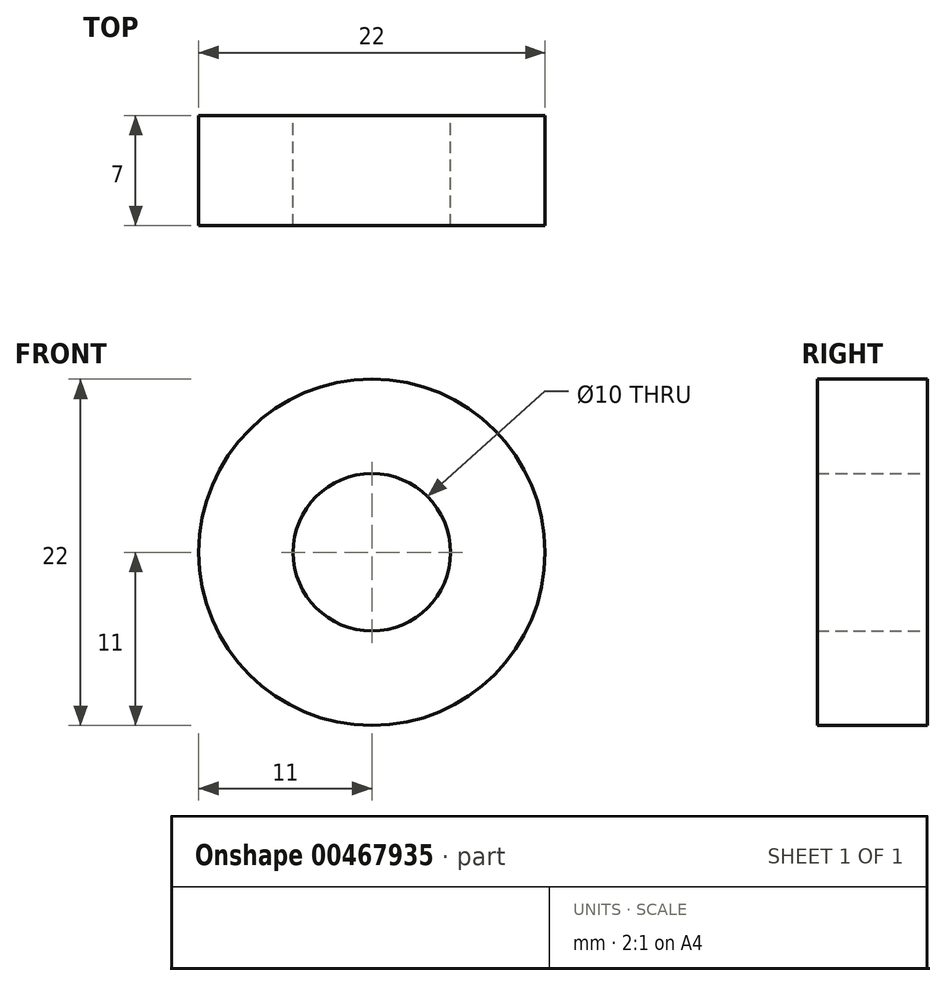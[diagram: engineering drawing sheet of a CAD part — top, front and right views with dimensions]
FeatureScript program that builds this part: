
annotation { "Feature Type Name" : "Feature", "Feature Type Description" : "" }
export const myFeature = defineFeature(function(context is Context, id is Id, definition is map)
    precondition{}
    {
        {
            var Q0;
            Q0=qCreatedBy(makeId("Front.planeOp"),FACE);
            var sketch = newSketch(context, id + "F0", { "sketchPlane" : qUnion([Q0])});
            skCircle(sketch, "E0", {"center": v(0, 0) * mm, "radius": 11 * mm});
            skCircle(sketch, "E1", {"center": v(0, 0) * mm, "radius": 4 * mm});
            skPoint(sketch, "E2", {"position": v(-4, 0) * mm});
            skPoint(sketch, "E3", {"position": v(0, 4) * mm});
            skPoint(sketch, "E4", {"position": v(4, 0) * mm});
            skPoint(sketch, "E5", {"position": v(0, -4) * mm});
            skPoint(sketch, "E6", {"position": v(0, -11) * mm});
            skPoint(sketch, "E7", {"position": v(-11, 0) * mm});
            skPoint(sketch, "E8", {"position": v(0, 11) * mm});
            skPoint(sketch, "E9", {"position": v(11, 0) * mm});
            skLineSegment(sketch, "E10", {"start": v(0, 4) * mm, "end": v(0, -4) * mm});
            skCircle(sketch, "E11", {"center": v(0, 0) * mm, "radius": 5 * mm});
            skCircle(sketch, "E12", {"center": v(0, 0) * mm, "radius": 10 * mm});
            skPoint(sketch, "E13", {"position": v(-5, 0) * mm});
            skPoint(sketch, "E14", {"position": v(-10, 0) * mm});
            skPoint(sketch, "E15", {"position": v(5, 0) * mm});
            skPoint(sketch, "E16", {"position": v(10, 0) * mm});
            skPoint(sketch, "E17", {"position": v(0, -5) * mm});
            skPoint(sketch, "E18", {"position": v(0, -10) * mm});
            skPoint(sketch, "E19", {"position": v(0, 5) * mm});
            skPoint(sketch, "E20", {"position": v(0, 10) * mm});
            skLineSegment(sketch, "E21", {"start": v(0, 5) * mm, "end": v(0, 10) * mm});
            skLineSegment(sketch, "E22", {"start": v(-4, 0) * mm, "end": v(-5, 0) * mm});
            skLineSegment(sketch, "E23", {"start": v(-10, 0) * mm, "end": v(-11, 0) * mm});
            skLineSegment(sketch, "E24", {"start": v(-11, 0) * mm, "end": v(11, 0) * mm});
            skSolve(sketch);
        }
        {
            var Q0;
            {var subQ0=sQuery(id+"F0.wireOp",EDGE,"E21");Q0=makeQuery(id+"F0.imprint","IMPRINT",FACE,{"disambiguationData":[TD([[makeQuery(id+"F0.imprint","IMPRINT",EDGE,{"derivedFrom":subQ0}),1.0]])]});}
            var Q1;
            {var subQ0=sQuery(id+"F0.wireOp",EDGE,"E24");var subQ1=sQuery(id+"F0.wireOp",EDGE,"E11");var subQ2=makeQuery(id+"F0.imprint","INTERSECT",VERTEX,{"disambiguationData":[OD(0.0)],"derivedFrom":[subQ1,subQ0]});Q1=makeQuery(id+"F0.imprint","IMPRINT",FACE,{"disambiguationData":[TD([[makeQuery(id+"F0.imprint","IMPRINT",EDGE,{"disambiguationData":[TD([[subQ2,1.0]])],"derivedFrom":subQ1}),-1.0]])]});}
            var Q2;
            {var subQ0=sQuery(id+"F0.wireOp",EDGE,"E21");Q2=makeQuery(id+"F0.imprint","IMPRINT",FACE,{"disambiguationData":[TD([[makeQuery(id+"F0.imprint","IMPRINT",EDGE,{"derivedFrom":subQ0}),-1.0]])]});}
            var Q3;
            {var subQ2=sQuery(id+"F0.wireOp",EDGE,"E24");var subQ5=sQuery(id+"F0.wireOp",EDGE,"E0");var subQ6=makeQuery(id+"F0.imprint","INTERSECT",VERTEX,{"disambiguationData":[OD(0.0)],"derivedFrom":[subQ5,subQ2]});Q3=makeQuery(id+"F0.imprint","IMPRINT",FACE,{"disambiguationData":[TD([[makeQuery(id+"F0.imprint","IMPRINT",EDGE,{"disambiguationData":[TD([[subQ6,1.0]])],"derivedFrom":subQ5}),1.0]])]});}
            var Q4;
            {var subQ0=sQuery(id+"F0.wireOp",EDGE,"E24");var subQ1=sQuery(id+"F0.wireOp",EDGE,"E0");var subQ2=makeQuery(id+"F0.imprint","INTERSECT",VERTEX,{"disambiguationData":[OD(0.0)],"derivedFrom":[subQ1,subQ0]});Q4=makeQuery(id+"F0.imprint","IMPRINT",FACE,{"disambiguationData":[TD([[makeQuery(id+"F0.imprint","IMPRINT",EDGE,{"disambiguationData":[TD([[subQ2,-1.0]])],"derivedFrom":subQ1}),1.0]])]});}
            extrude(context, id + "F1", {"entities" : qUnion([Q0, Q1, Q2, Q3, Q4]), "depth" : 7 * mm});
        }
    });
